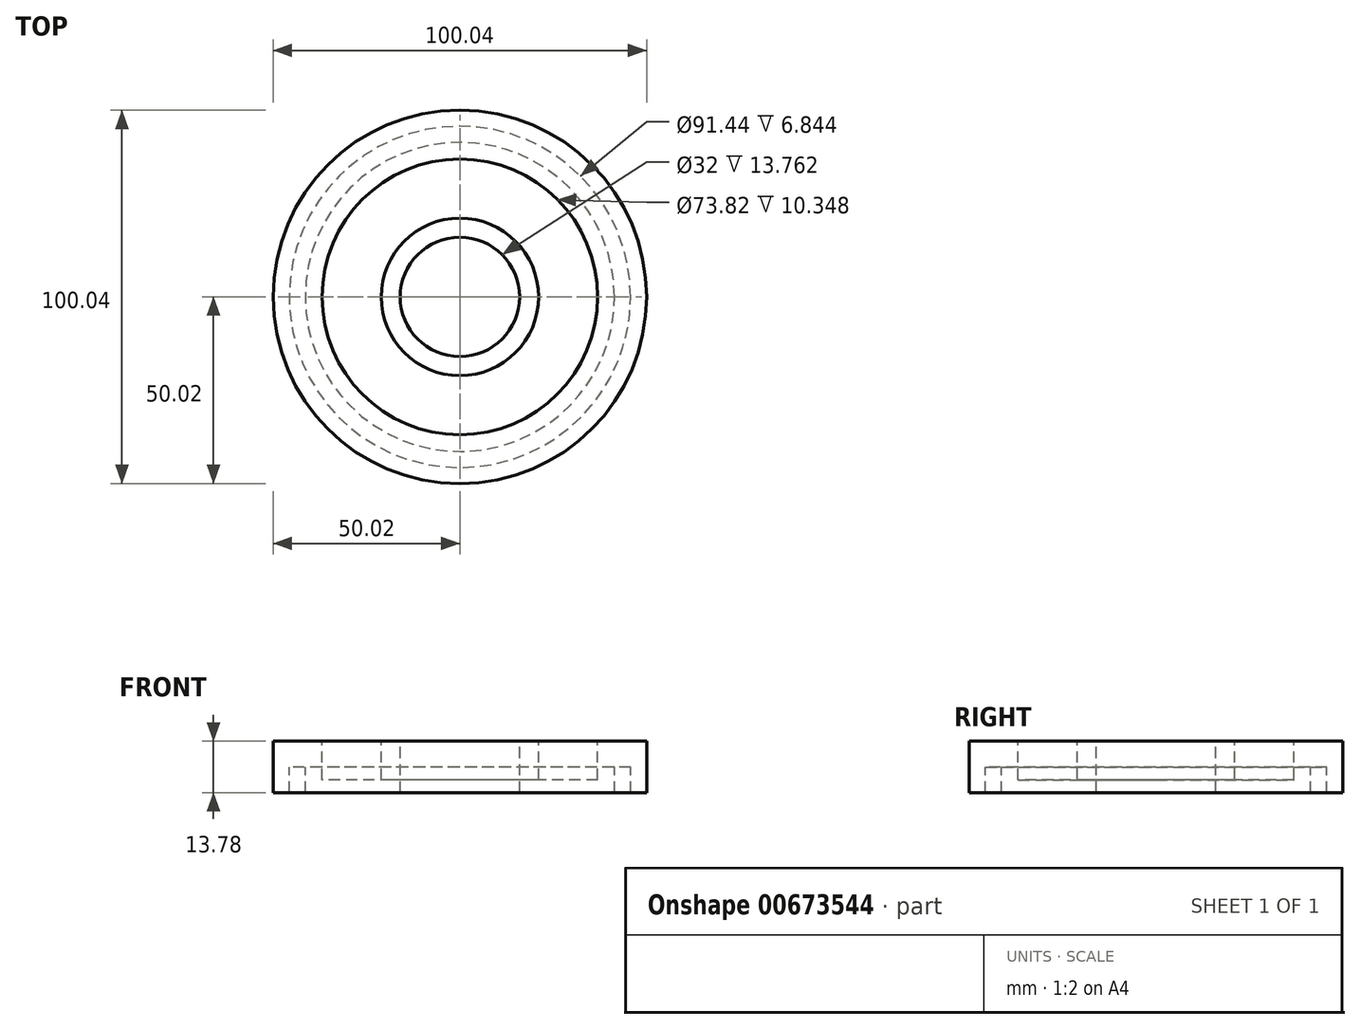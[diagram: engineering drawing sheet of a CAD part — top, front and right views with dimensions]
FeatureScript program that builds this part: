
annotation { "Feature Type Name" : "Feature", "Feature Type Description" : "" }
export const myFeature = defineFeature(function(context is Context, id is Id, definition is map)
    precondition{}
    {
        {
            var Q0;
            Q0=qCreatedBy(makeId("Front.planeOp"),FACE);
            var sketch = newSketch(context, id + "F0", { "sketchPlane" : qUnion([Q0])});
            skLineSegment(sketch, "E0", {"start": v(-50.02, 8.98) * mm, "end": v(-36.9, 8.98) * mm});
            skLineSegment(sketch, "E1", {"start": v(-36.9, 8.98) * mm, "end": v(-36.9, -1.37) * mm});
            skLineSegment(sketch, "E2", {"start": v(-36.9, -1.37) * mm, "end": v(-21.08, -1.37) * mm});
            skLineSegment(sketch, "E3", {"start": v(-21.08, -1.37) * mm, "end": v(-21.08, 3.67) * mm});
            skLineSegment(sketch, "E4", {"start": v(-21.08, 3.67) * mm, "end": v(-21.08, 8.98) * mm});
            skLineSegment(sketch, "E5", {"start": v(-21.08, 8.98) * mm, "end": v(-16, 8.98) * mm});
            skLineSegment(sketch, "E6", {"start": v(-16, 8.98) * mm, "end": v(-16, -4.78) * mm});
            skLineSegment(sketch, "E7", {"start": v(-16, -4.78) * mm, "end": v(-41.4, -4.78) * mm});
            skLineSegment(sketch, "E8", {"start": v(-41.4, -4.78) * mm, "end": v(-41.4, 2.04) * mm});
            skLineSegment(sketch, "E9", {"start": v(-41.4, 2.04) * mm, "end": v(-45.72, 2.04) * mm});
            skLineSegment(sketch, "E10", {"start": v(-45.72, 2.04) * mm, "end": v(-45.72, -4.8) * mm});
            skLineSegment(sketch, "E11", {"start": v(-45.72, -4.8) * mm, "end": v(-50.02, -4.8) * mm});
            skPoint(sketch, "E12.start.orphan", {"position": v(-50.02, -3.64) * mm});
            skLineSegment(sketch, "E13", {"start": v(-50.02, 8.98) * mm, "end": v(-50.02, -4.8) * mm});
            skLineSegment(sketch, "E14", {"start": v(0, 46.5) * mm, "end": v(0, -29.96) * mm});
            skSolve(sketch);
        }
        {
            var Q0;
            Q0=makeQuery(id+"F0.imprint","IMPRINT",FACE,{"disambiguationData":[TD([[makeQuery(id+"F0.imprint","IMPRINT",EDGE,{"derivedFrom":sQuery(id+"F0.wireOp",EDGE,"E0")}),-1.0]])]});
            var Q1;
            Q1=sQuery(id+"F0.wireOp",EDGE,"E14");
            revolve(context, id + "F1", {"entities" : qUnion([Q0]), "axis" : qUnion([Q1]), "revolveType" : RevolveType.FULL});
        }
    });
